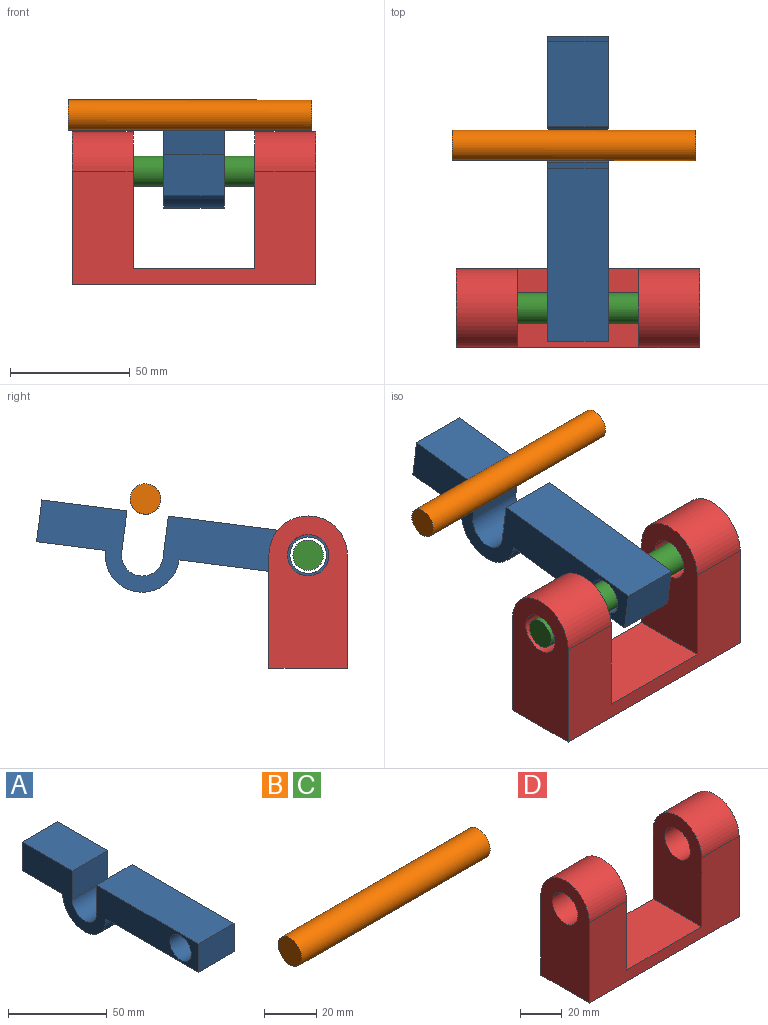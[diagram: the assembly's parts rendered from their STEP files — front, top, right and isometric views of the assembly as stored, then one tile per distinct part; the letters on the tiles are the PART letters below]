
ASSEMBLY  parts=4 mates=2
PART A: 13 faces, bbox 25.4x126.1x33 mm
  f0: plane 25.4x17.56mm, normal (0,1,0), area 445.9mm2, adj f1,f9,f10,f11
  f1: plane 72.82x25.4mm, normal (0,0,1), area 1849.5mm2, adj f0,f2,f10,f11
  f2: plane 25.4x17.56mm, normal (0,-1,0), area 445.9mm2, adj f1,f3,f10,f11
  f3: plane 66.05x25.4mm, normal (0,0,-1), area 1677.7mm2, adj f2,f4,f10,f11
  f4: cylinder r=15.47mm len=30.94mm, axis (-1,0,0), area 1234.4mm2, adj f3,f5,f10,f11
  f5: plane 29.07x25.4mm, normal (0,0,-1), area 738.3mm2, adj f4,f6,f10,f11
  f6: plane 25.4x17.56mm, normal (0,1,0), area 445.9mm2, adj f5,f7,f10,f11
  f7: plane 35.83x25.4mm, normal (0,0,1), area 910.1mm2, adj f6,f8,f10,f11
  f8: plane 25.4x17.56mm, normal (0,-1,0), area 445.9mm2, adj f7,f9,f10,f11
  f9: cylinder r=8.71mm len=25.4mm, axis (-1,0,0), area 694.7mm2, adj f0,f8,f10,f11
  f10: plane 126.06x33.03mm, normal (1,0,0), area 1981.8mm2, adj f0,f1,f2,f3,f4,f5,f6,f7
  f11: plane 126.06x33.03mm, normal (-1,0,0), area 1981.8mm2, adj f0,f1,f2,f3,f4,f5,f6,f7
  f12: cylinder r=7.62mm len=25.4mm, axis (-1,0,0), area 1216.1mm2, adj f10,f11
PART B: 3 faces, bbox 101.6x12.7x12.7 mm
  f0: cylinder r=6.35mm len=101.6mm, axis (-1,0,0), area 4053.7mm2, adj f1,f2
  f1: plane 12.7x12.7mm, normal (1,0,0), area 126.7mm2, adj f0
  f2: plane 12.7x12.7mm, normal (-1,0,0), area 126.7mm2, adj f0
PART C: same geometry as B
PART D: 12 faces, bbox 101.6x32.8x63.6 mm
  f0: plane 101.6x47.2mm, normal (0,1,0), area 2737mm2, adj f1,f2,f6,f7,f8,f9,f10,f11
  f1: cylinder r=16.4mm len=32.81mm, axis (1,0,0), area 1309.1mm2, adj f0,f5,f8,f9
  f2: cylinder r=16.4mm len=32.81mm, axis (1,0,0), area 1309.1mm2, adj f0,f5,f7,f10
  f3: cylinder r=8.65mm len=25.4mm, axis (1,0,0), area 1380.2mm2, adj f8,f9
  f4: cylinder r=8.65mm len=25.4mm, axis (1,0,0), area 1380.2mm2, adj f7,f10
  f5: plane 101.6x47.2mm, normal (0,-1,0), area 2737mm2, adj f1,f2,f6,f7,f8,f9,f10,f11
  f6: plane 101.6x32.81mm, normal (0,0,-1), area 3333.5mm2, adj f0,f5,f7,f8
  f7: plane 63.61x32.81mm, normal (-1,0,0), area 1736.4mm2, adj f0,f2,f4,f5,f6
  f8: plane 63.61x32.81mm, normal (1,0,0), area 1736.4mm2, adj f0,f1,f3,f5,f6
  f9: plane 56.93x32.81mm, normal (-1,0,0), area 1517.3mm2, adj f0,f1,f3,f5,f11
  f10: plane 56.93x32.81mm, normal (1,0,0), area 1517.3mm2, adj f0,f2,f4,f5,f11
  f11: plane 50.8x32.81mm, normal (0,0,1), area 1666.7mm2, adj f0,f5,f9,f10
PLACE A rot(axis=(1,0,0),7.3deg) t=(-83.32,48.19,-18.81)mm
PLACE B rot(axis=(-1,0,0),180deg) t=(-123,61.79,10.34)mm
PLACE C t=(-121.42,-6.2,-13.15)mm
PLACE D t=(-19.82,-6.91,-51.14)mm fixed
MATE fastened C.f0 <-> D.f1  axis (-1,0,0) through (-19.82,-6.2,-13.15)mm
MATE revolute A.f12 <-> C.f0  axis (-1,0,0) through (-70.62,-6.2,-13.15)mm
